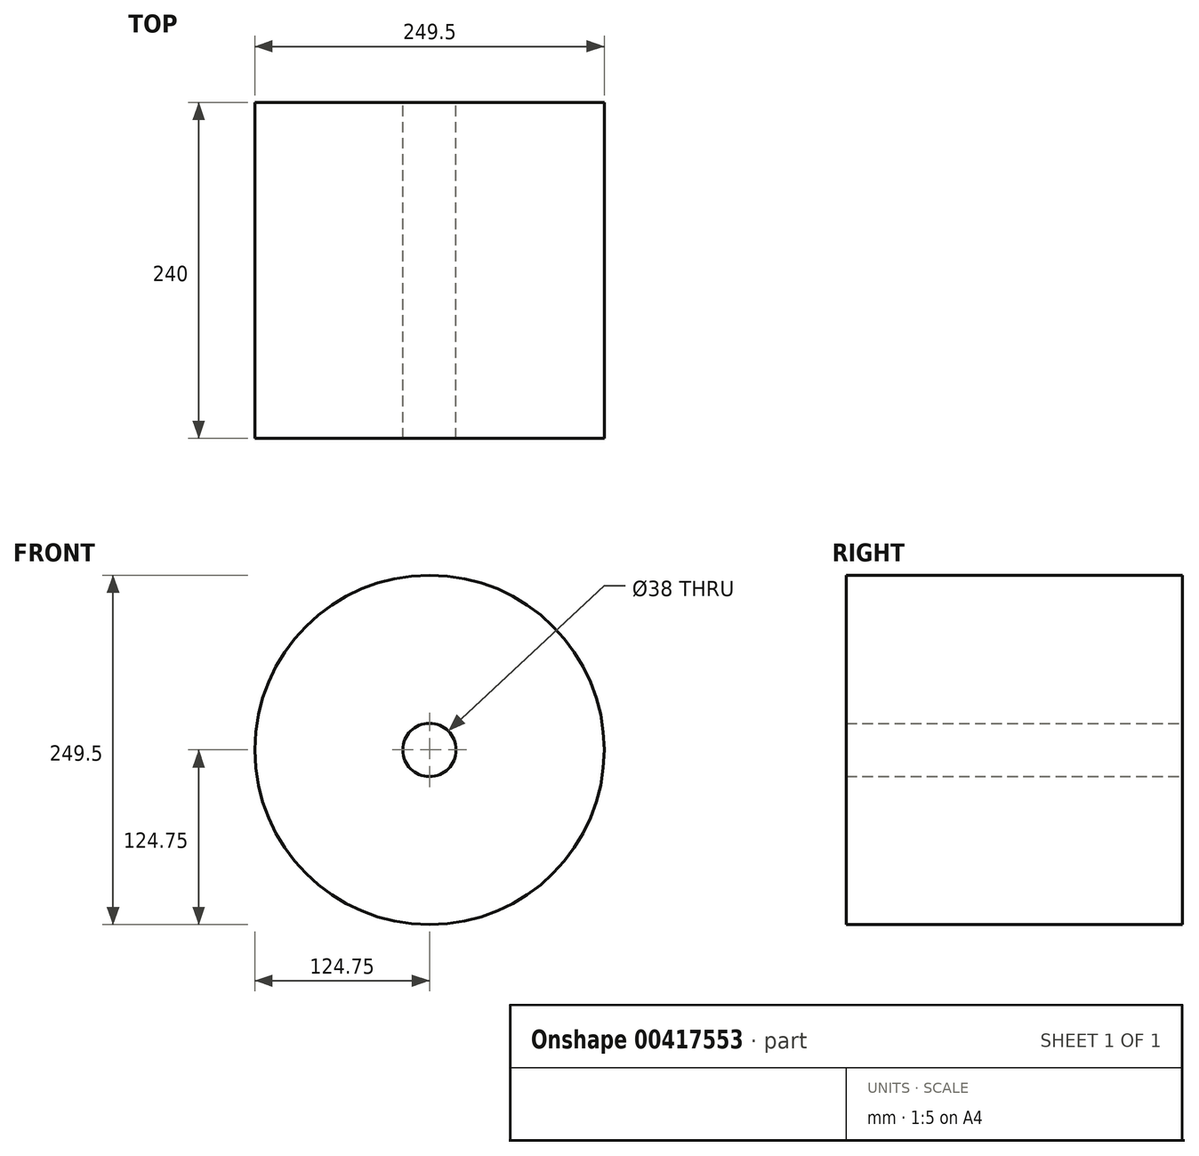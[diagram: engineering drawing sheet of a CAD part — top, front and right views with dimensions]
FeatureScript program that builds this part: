
annotation { "Feature Type Name" : "Feature", "Feature Type Description" : "" }
export const myFeature = defineFeature(function(context is Context, id is Id, definition is map)
    precondition{}
    {
        {
            var Q0;
            Q0=qCreatedBy(makeId("Front.planeOp"),FACE);
            var sketch = newSketch(context, id + "F0", { "sketchPlane" : qUnion([Q0])});
            skCircle(sketch, "E0", {"center": v(0, 0) * mm, "radius": 124.75 * mm});
            skCircle(sketch, "E1", {"center": v(0, 0) * mm, "radius": 19 * mm});
            skSolve(sketch);
        }
        {
            var Q0;
            Q0=makeQuery(id+"F0.imprint","IMPRINT",FACE,{"disambiguationData":[TD([[makeQuery(id+"F0.imprint","IMPRINT",EDGE,{"derivedFrom":sQuery(id+"F0.wireOp",EDGE,"E0")}),1.0]])]});
            extrude(context, id + "F1", {"entities" : qUnion([Q0]), "depth" : 240 * mm});
        }
    });
